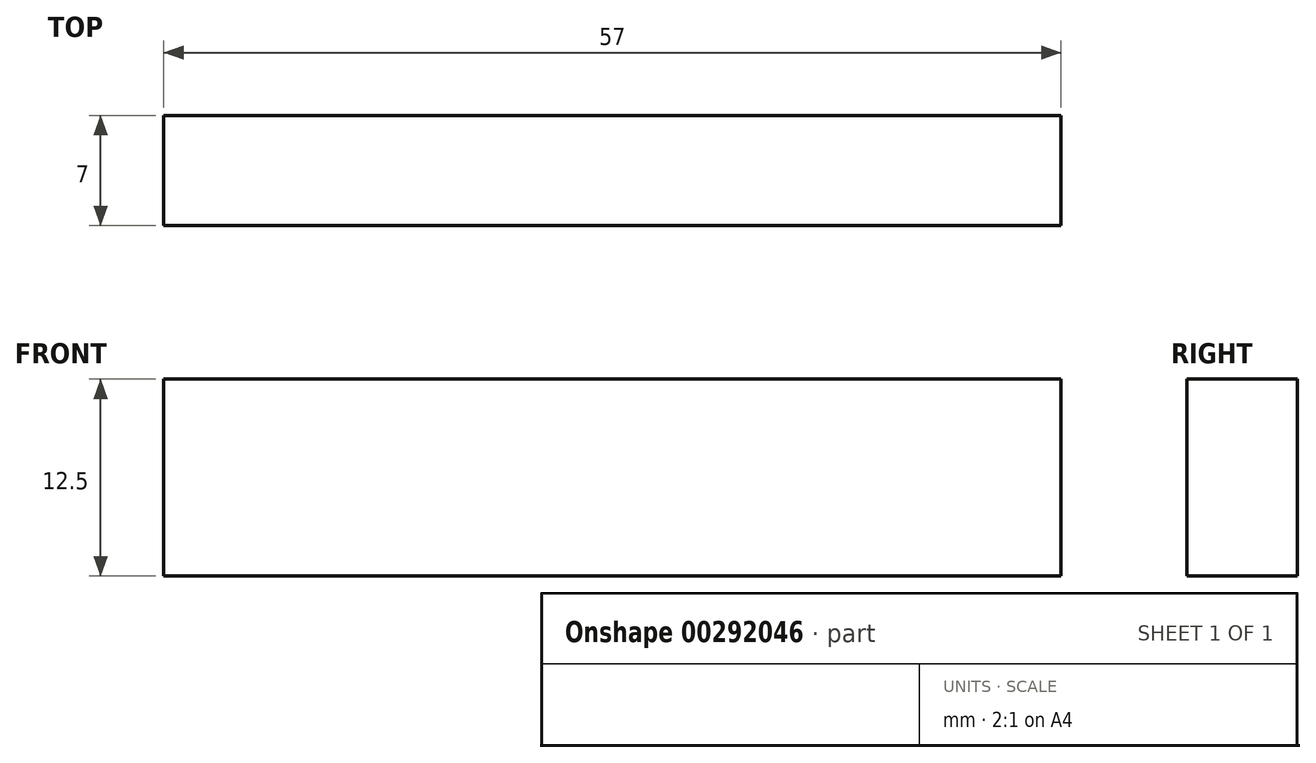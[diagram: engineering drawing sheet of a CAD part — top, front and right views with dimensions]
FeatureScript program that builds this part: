
annotation { "Feature Type Name" : "Feature", "Feature Type Description" : "" }
export const myFeature = defineFeature(function(context is Context, id is Id, definition is map)
    precondition{}
    {
        {
            var Q0;
            Q0=qCreatedBy(makeId("Front.planeOp"),FACE);
            var sketch = newSketch(context, id + "F0", { "sketchPlane" : qUnion([Q0])});
            skLineSegment(sketch, "E0", {"start": v(0, 6.25) * mm, "end": v(28.5, 6.25) * mm});
            skLineSegment(sketch, "E1", {"start": v(28.5, 6.25) * mm, "end": v(28.5, 0) * mm});
            skLineSegment(sketch, "E2.MirrorCS", {"start": v(0, 6.25) * mm, "end": v(-28.5, 6.25) * mm});
            skLineSegment(sketch, "E3.MirrorCS", {"start": v(-28.5, 6.25) * mm, "end": v(-28.5, 0) * mm});
            skLineSegment(sketch, "E4.MirrorCS", {"start": v(-28.5, -6.25) * mm, "end": v(-28.5, 0) * mm});
            skLineSegment(sketch, "E5.MirrorCS", {"start": v(28.5, -6.25) * mm, "end": v(28.5, 0) * mm});
            skLineSegment(sketch, "E6.MirrorCS", {"start": v(0, -6.25) * mm, "end": v(-28.5, -6.25) * mm});
            skLineSegment(sketch, "E7.MirrorCS", {"start": v(0, -6.25) * mm, "end": v(28.5, -6.25) * mm});
            skSolve(sketch);
        }
        {
            var Q0;
            Q0 = qSketchRegion(id + "F0", true);
            extrude(context, id + "F1", {"entities" : qUnion([Q0]), "endBound" : BoundingType.SYMMETRIC, "depth" : 7 * mm});
        }
    });
